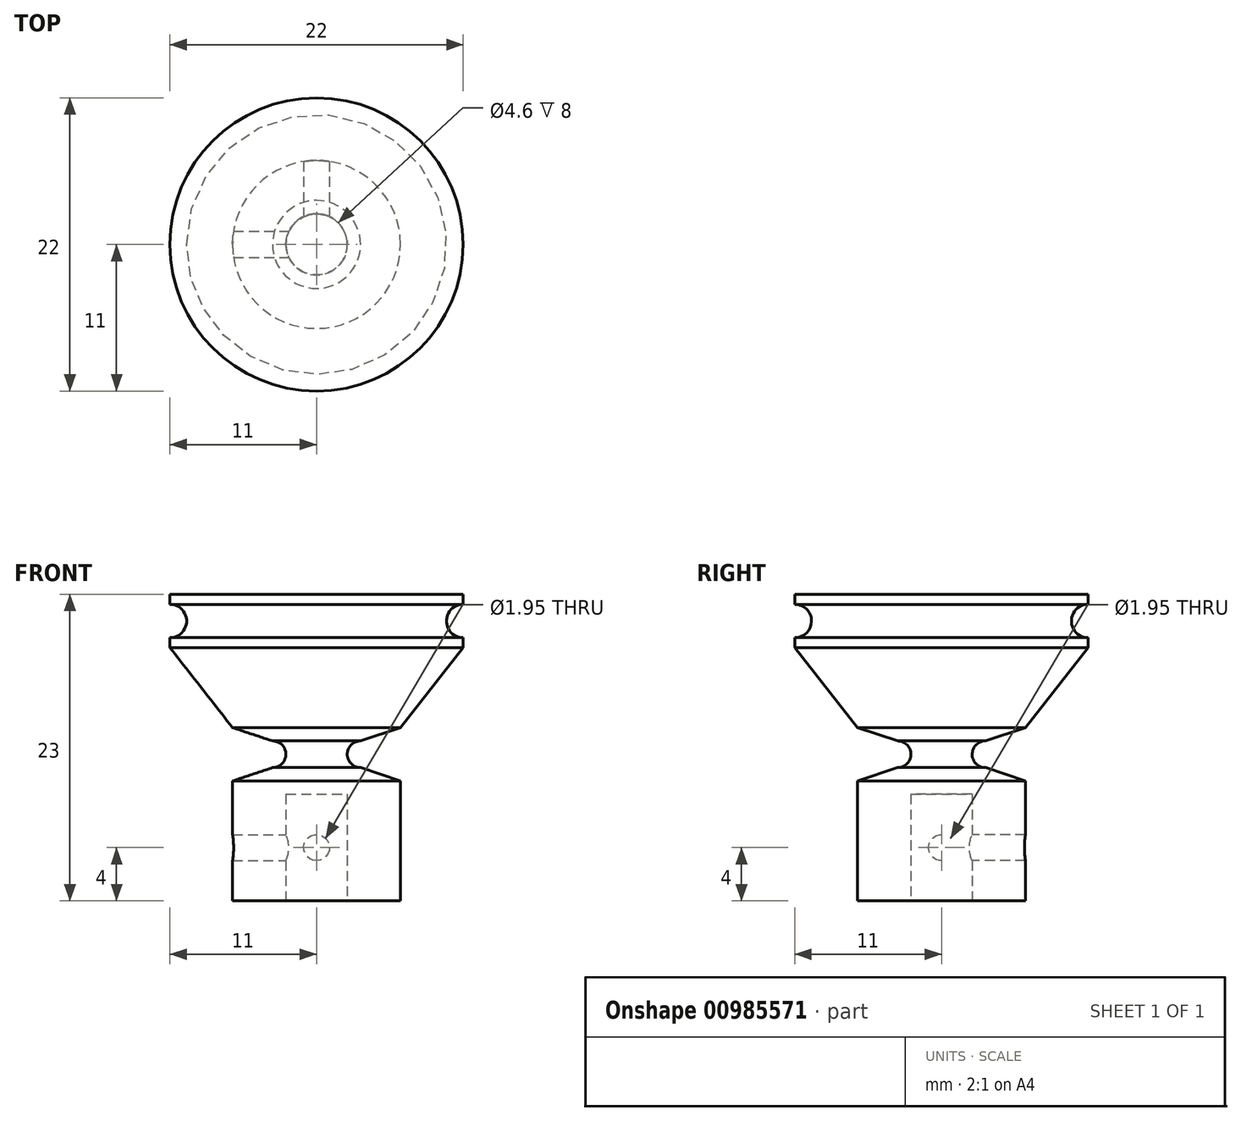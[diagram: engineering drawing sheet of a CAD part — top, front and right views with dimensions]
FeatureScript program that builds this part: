
annotation { "Feature Type Name" : "Feature", "Feature Type Description" : "" }
export const myFeature = defineFeature(function(context is Context, id is Id, definition is map)
    precondition{}
    {
        {
            var Q0;
            Q0=qCreatedBy(makeId("Front.planeOp"),FACE);
            var sketch = newSketch(context, id + "F0", { "sketchPlane" : qUnion([Q0])});
            skLineSegment(sketch, "E0", {"start": v(0, 0) * mm, "end": v(-2.3, 0) * mm, "construction": true});
            skLineSegment(sketch, "E1", {"start": v(-2.3, 0) * mm, "end": v(-2.3, 8) * mm});
            skLineSegment(sketch, "E2", {"start": v(-2.3, 8) * mm, "end": v(0, 8) * mm});
            skLineSegment(sketch, "E3", {"start": v(0, 8) * mm, "end": v(0, 23) * mm});
            skLineSegment(sketch, "E4", {"start": v(0, 23) * mm, "end": v(-11, 23) * mm});
            skLineSegment(sketch, "E5", {"start": v(-2.3, 0) * mm, "end": v(-6.3, 0) * mm});
            skLineSegment(sketch, "E6", {"start": v(-11, 23) * mm, "end": v(-11, 22.25) * mm});
            skLineSegment(sketch, "E7", {"start": v(-11, 19.75) * mm, "end": v(-11, 19) * mm});
            skPoint(sketch, "E8", {"position": v(-9.75, 21) * mm});
            skArc(sketch, "E9", {"start": v(-11, 19.75) * mm, "mid": v(-9.75, 21) * mm, "end": v(-11, 22.25) * mm});
            skPoint(sketch, "E10", {"position": v(-2.3, 11) * mm});
            skArc(sketch, "E11", {"start": v(-3.3, 10) * mm, "mid": v(-2.3, 11) * mm, "end": v(-3.3, 12) * mm});
            skLineSegment(sketch, "E12", {"start": v(-6.3, 0) * mm, "end": v(-6.3, 9) * mm});
            skLineSegment(sketch, "E13", {"start": v(-3.3, 10) * mm, "end": v(-6.3, 9) * mm});
            skLineSegment(sketch, "E14", {"start": v(-6.3, 9) * mm, "end": v(-6.3, 13) * mm, "construction": true});
            skLineSegment(sketch, "E15", {"start": v(-6.3, 13) * mm, "end": v(-3.3, 12) * mm});
            skLineSegment(sketch, "E16", {"start": v(-6.3, 13) * mm, "end": v(-11, 19) * mm});
            skPoint(sketch, "E17", {"position": v(0, 4) * mm});
            skCircle(sketch, "E18", {"center": v(0, 4) * mm, "radius": 0.97 * mm});
            skSolve(sketch);
        }
        {
            var Q0;
            Q0=makeQuery(id+"F0.imprint","IMPRINT",FACE,{"disambiguationData":[TD([[makeQuery(id+"F0.imprint","IMPRINT",EDGE,{"derivedFrom":sQuery(id+"F0.wireOp",EDGE,"E1")}),1.0]])]});
            var Q1;
            Q1=sQuery(id+"F0.wireOp",EDGE,"E3");
            revolve(context, id + "F1", {"surfaceOperationType" : NewSurfaceOperationType.NEW, "entities" : qUnion([Q0]), "axis" : qUnion([Q1]), "revolveType" : RevolveType.FULL});
        }
        {
            var Q0;
            Q0=makeQuery(id+"F0.imprint","IMPRINT",FACE,{"disambiguationData":[TD([[makeQuery(id+"F0.imprint","IMPRINT",EDGE,{"derivedFrom":sQuery(id+"F0.wireOp",EDGE,"E18")}),1.0]])]});
            extrude(context, id + "F2", {"entities" : qUnion([Q0]), "operationType" : NewBodyOperationType.REMOVE, "oppositeDirection" : true, "depth" : 6.6 * mm, "offsetDistance" : 25 * mm});
        }
        {
            var Q0;
            Q0=qCreatedBy(makeId("Right.planeOp"),FACE);
            var sketch = newSketch(context, id + "F3", { "sketchPlane" : qUnion([Q0])});
            skCircle(sketch, "E19", {"center": v(0, 4) * mm, "radius": 0.98 * mm});
            skSolve(sketch);
        }
        {
            var Q0;
            Q0=makeQuery(id+"F3.imprint","IMPRINT",FACE,{"disambiguationData":[TD([[makeQuery(id+"F3.imprint","IMPRINT",EDGE,{"derivedFrom":sQuery(id+"F3.wireOp",EDGE,"E19")}),1.0]])]});
            extrude(context, id + "F4", {"entities" : qUnion([Q0]), "operationType" : NewBodyOperationType.REMOVE, "oppositeDirection" : true, "depth" : 6.6 * mm, "offsetDistance" : 25 * mm});
        }
    });
